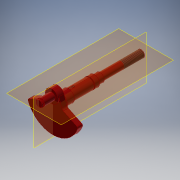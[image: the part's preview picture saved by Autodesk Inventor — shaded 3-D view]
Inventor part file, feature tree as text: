
AUTODESK INVENTOR PART (.ipt)
format: ipt  version: 2018 (Build 220112000, 112)  size: 222,720 bytes
history: native  units: mm
features: sketch x7, extrude x6, revolve x1, chamfer x1, thread x1, plane x1
ambient origin geometry x8: Origin, YZ Plane, XZ Plane, XY Plane, X Axis, Y Axis, Z Axis, Center Point
bodies: Solid1 (feature_tree)
feature tree (17):
  revolve  "Revolution1"  [1 undecoded]
  extrude  "Extrusion1"  Depth=5.0mm
  extrude  "Extrusion2"  Depth=7.5mm
  extrude  "Extrusion3"  Depth=2.5mm
  extrude  "Extrusion4"  Depth=1.25mm
  extrude  "Extrusion5"  Depth=57.0mm
  chamfer  "Chamfer1"  Distance=28.5mm
  thread  "Thread1"  [1 undecoded]
  plane  "Work Plane1"
  extrude  "Extrusion6"  Depth=1.5mm
  sketch  "Sketch1"  dims[d0=5.0mm d1=6.0mm]
  sketch  "Sketch2"  dims[d2=7.5mm d3=5.0mm]
  sketch  "Sketch3"  dims[d4=8.5mm d5=7.5mm]
  sketch  "Sketch4"  dims[d6=11.0mm d7=2.5mm]
  sketch  "Sketch5"  dims[d8=12.0mm d9=1.25mm]
  sketch  "Sketch6"  dims[d10=6.25mm d12=57.0mm]
  sketch  "Sketch7"  dims[d13=65.0mm d14=28.5mm d15=90.0deg d16=18.0mm d17=73.0mm d18=10.64mm d19=3.141593mm d20=4.45059mm d21=4.0mm d22=2.0mm d24=56.14mm d25=3.141593mm d26=4.45059mm d27=7.0mm d28=0.0mm d29=1.5mm d30=0.0mm d31=10.0mm d32=15.0mm d33=0.0mm d35=9.0mm d36=1.1mm d37=0.0mm d38=10.0mm d39=1.6mm d40=0.0mm d41=0.8mm d42=2.0mm d43=45.0deg d44=28.0mm d45=0.0mm d46=1.5mm d47=5.0mm d48=0.5mm d49=2.0mm d50=0.0mm]
note: 2 required parameter values undecoded (feature->parameter linkage not recoverable at this tier; creation-order binding heuristic only, values carry confidence <= 0.55)